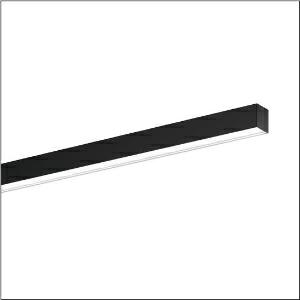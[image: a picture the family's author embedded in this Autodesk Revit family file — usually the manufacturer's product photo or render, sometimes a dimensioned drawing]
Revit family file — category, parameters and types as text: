
# Revit family: silica_r__21_51mx23da44bb_c0fe
name_source: partatom
category: Lighting Fixtures
units: mm (PartAtom-declared; Revit-internal decimal feet)

## family parameters
Cut with Voids When Loaded = No
Host = Face
Light Source = No
Part Type = Normal
Room Calculation Point = No
Round Connector Dimension = Use Diameter
Shared = No

## types (1)
- --- (1 x LED, 3280 lm, 22.4 W, 4000K)
    Apparent Load = 22 VA
    CIE Flux Codes = 78 96 99 100 100
    Color Rendering = 80
    Color Temperature = 4000K
    Default Elevation = 1800 mm
    Description = Silica® 21, office luminaire, primary optical cover: prismatic diffuser, of PMMA, CAT 2 (L<= 3000cd/m²), light emission: direct distribution, primary light characteristic: symmetric, installation type: surface-mounted, LED, rated luminous flux: 3.280lm, luminous efficacy: 146lm/W, light colour: 840, colour temperature: 4000K, with terminal, 3+2-pole, max. 2.5mm², mains connection: 220..240V, AC, 50/60Hz, rated input power: 22.4W, luminaire housing, of aluminium, jet black (RAL 9005), length: 1.204mm, width: 53mm, height: 53mm, protection rating (complete): IP20, insulation class (complete): insulation class I (protective earthing), certification: CE, permissible operating ambient temperature: 0..+35°C, standard: EN 50419, packaging unit: 1 piece
    Height = 0 mm  [stored 0 ft]
    Lamp = 1 x LED
    Lamp Light Flux = 3280 lm
    Lamp Power = 22.4 W
    Lamp count = 1
    Length = 1204 mm
    Luminous efficacy = 146 lm/W
    Manufacturer = Siteco
    ModVariant = No
    Model = 51MX23DA44BB
    Mounting Place = Ceiling
    Mounting Type = Recessed
    Number of Poles = 1
    OnlyDefault = Yes
    Power Factor = 1
    Product Name = Silica® 21
    Product group = office luminaire | ceiling recessed
    ProductGroupID = 401
    Protection Class = Protection class I
    Protection Degree = IP 20
    RLX_Detail_Level = 1
    RLX_Emergency_Light_Flux = 0 lm
    RLX_Emergency_Type = 0
    RLX_Emergency_Type_DB = No
    RlxData = <blob elided: 23657 chars, md5=c8bf6324>
    Socket = socket
    Standby Power = 0 W
    System Light Flux = 3280 lm
    System Power = 22 W
    Type Comments = factory setting: luminous flux: 100 % | dim-lin: 254 | 323 mA
    Type Image = l_1297760.jpg
    URL = http://relux.com
    VarID = @adj_050033
    Voltage = 0 V
    Weight = 0.00 kg
    Width = 53 mm

note: [stored X ft] marks values corroborated as IEEE doubles in the binary element streams (Revit-internal decimal feet)

## geometry (parser evidence)
native form markers: Blend x4, Sweep x11
no freeform markers — native parametric forms only
